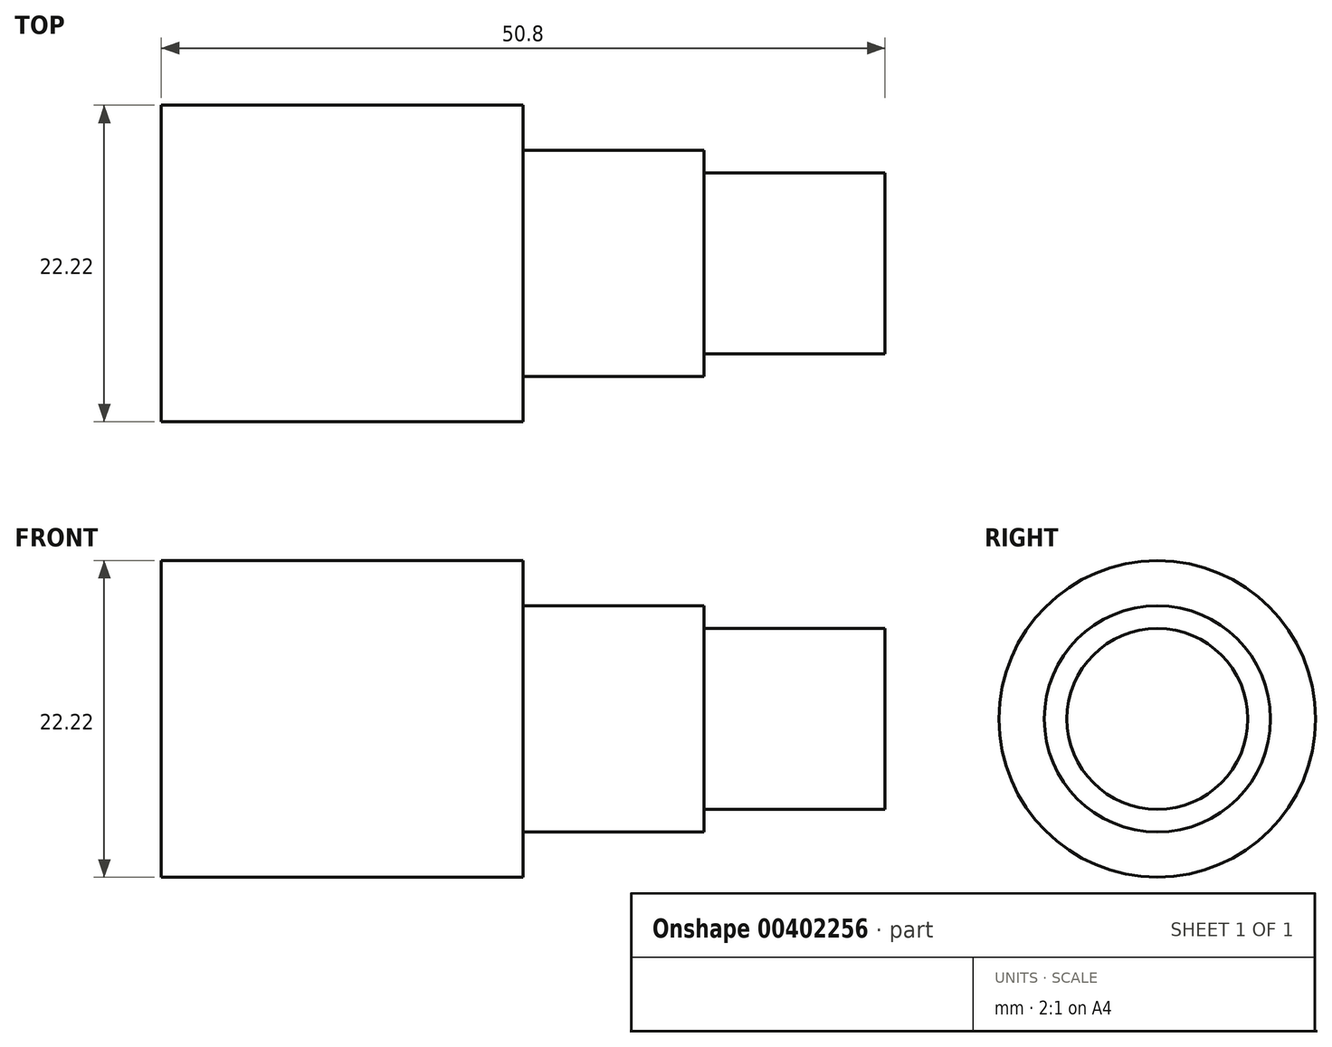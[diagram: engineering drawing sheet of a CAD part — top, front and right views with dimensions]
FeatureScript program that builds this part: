
annotation { "Feature Type Name" : "Feature", "Feature Type Description" : "" }
export const myFeature = defineFeature(function(context is Context, id is Id, definition is map)
    precondition{}
    {
        {
            var Q0;
            Q0=qCreatedBy(makeId("Front.planeOp"),FACE);
            var sketch = newSketch(context, id + "F0", { "sketchPlane" : qUnion([Q0])});
            skLineSegment(sketch, "E0", {"start": v(0, 0) * mm, "end": v(50.8, 0) * mm});
            skLineSegment(sketch, "E1", {"start": v(0, 0) * mm, "end": v(0, 11.11) * mm});
            skLineSegment(sketch, "E2", {"start": v(0, 11.11) * mm, "end": v(25.4, 11.11) * mm});
            skLineSegment(sketch, "E3", {"start": v(25.4, 11.11) * mm, "end": v(25.4, 7.94) * mm});
            skLineSegment(sketch, "E4", {"start": v(25.4, 7.94) * mm, "end": v(38.1, 7.94) * mm});
            skLineSegment(sketch, "E5", {"start": v(38.1, 7.94) * mm, "end": v(38.1, 6.35) * mm});
            skLineSegment(sketch, "E6", {"start": v(38.1, 6.35) * mm, "end": v(50.8, 6.35) * mm});
            skLineSegment(sketch, "E7", {"start": v(50.8, 6.35) * mm, "end": v(50.8, 0) * mm});
            skSolve(sketch);
        }
        {
            var Q0;
            Q0 = qSketchRegion(id + "F0", true);
            var Q1;
            Q1=sQuery(id+"F0.wireOp",EDGE,"E0");
            revolve(context, id + "F1", {"entities" : qUnion([Q0]), "axis" : qUnion([Q1]), "revolveType" : RevolveType.FULL});
        }
    });
